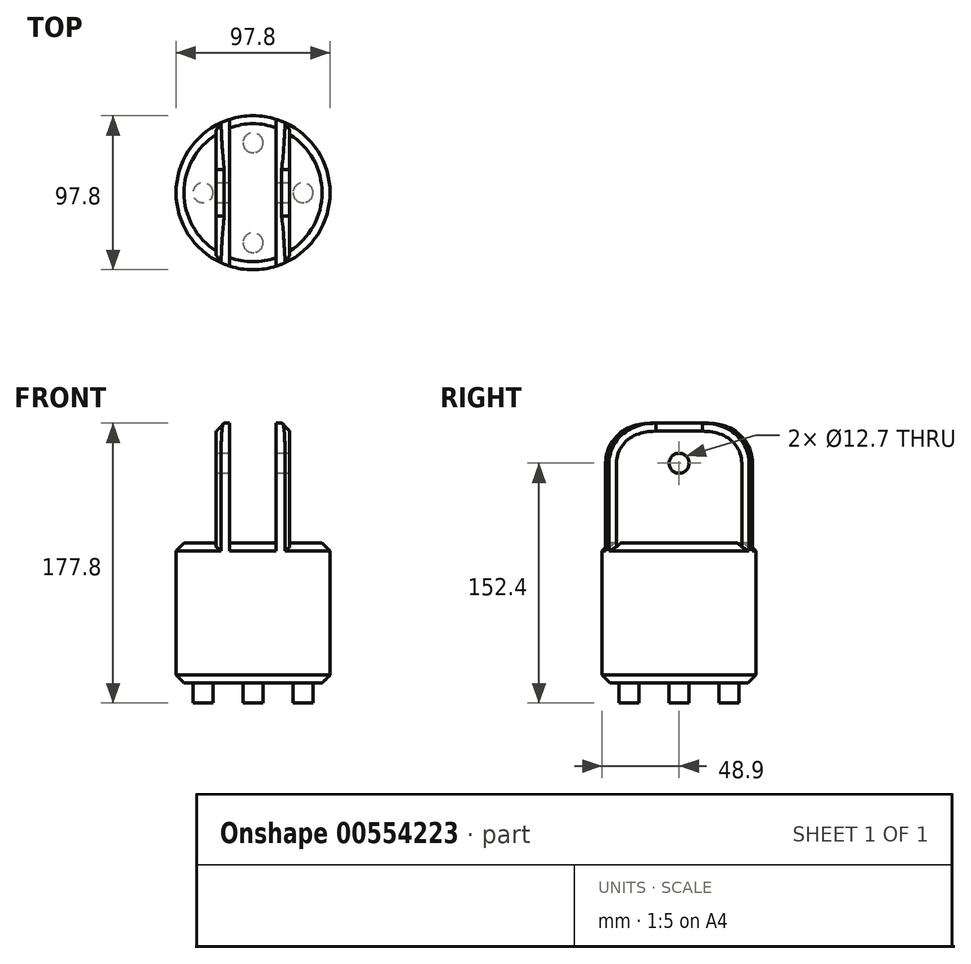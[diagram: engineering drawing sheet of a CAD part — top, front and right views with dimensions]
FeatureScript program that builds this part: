
annotation { "Feature Type Name" : "Feature", "Feature Type Description" : "" }
export const myFeature = defineFeature(function(context is Context, id is Id, definition is map)
    precondition{}
    {
        {
            var Q0;
            Q0=qCreatedBy(makeId("Top.planeOp"),FACE);
            var sketch = newSketch(context, id + "F0", { "sketchPlane" : qUnion([Q0])});
            skCircle(sketch, "E0", {"center": v(0, 0) * mm, "radius": 48.9 * mm});
            skCircle(sketch, "E1", {"center": v(0, 0) * mm, "radius": 31.75 * mm});
            skCircle(sketch, "E2", {"center": v(0, -31.75) * mm, "radius": 6.35 * mm});
            skCircle(sketch, "E3", {"center": v(-31.75, 0) * mm, "radius": 6.35 * mm});
            skCircle(sketch, "E4", {"center": v(31.75, 0) * mm, "radius": 6.35 * mm});
            skCircle(sketch, "E5", {"center": v(0, 31.75) * mm, "radius": 6.35 * mm});
            skSolve(sketch);
        }
        {
            var Q0;
            Q0=makeQuery(id+"F0.imprint","IMPRINT",FACE,{"disambiguationData":[TD([[makeQuery(id+"F0.imprint","IMPRINT",EDGE,{"derivedFrom":sQuery(id+"F0.wireOp",EDGE,"E0")}),1.0]])]});
            var Q1;
            {var subQ0=sQuery(id+"F0.wireOp",EDGE,"E3");var subQ1=sQuery(id+"F0.wireOp",EDGE,"E1");var subQ2=makeQuery(id+"F0.imprint","INTERSECT",VERTEX,{"disambiguationData":[OD(0.0)],"derivedFrom":[subQ1,subQ0]});Q1=makeQuery(id+"F0.imprint","IMPRINT",FACE,{"disambiguationData":[TD([[makeQuery(id+"F0.imprint","IMPRINT",EDGE,{"disambiguationData":[TD([[subQ2,-1.0]])],"derivedFrom":subQ1}),1.0]])]});}
            var Q2;
            {var subQ0=sQuery(id+"F0.wireOp",EDGE,"E5");var subQ1=sQuery(id+"F0.wireOp",EDGE,"E1");var subQ2=makeQuery(id+"F0.imprint","INTERSECT",VERTEX,{"disambiguationData":[OD(0.0)],"derivedFrom":[subQ1,subQ0]});Q2=makeQuery(id+"F0.imprint","IMPRINT",FACE,{"disambiguationData":[TD([[makeQuery(id+"F0.imprint","IMPRINT",EDGE,{"disambiguationData":[TD([[subQ2,-1.0]])],"derivedFrom":subQ1}),-1.0]])]});}
            var Q3;
            {var subQ0=sQuery(id+"F0.wireOp",EDGE,"E5");var subQ1=sQuery(id+"F0.wireOp",EDGE,"E1");var subQ2=makeQuery(id+"F0.imprint","INTERSECT",VERTEX,{"disambiguationData":[OD(0.0)],"derivedFrom":[subQ1,subQ0]});Q3=makeQuery(id+"F0.imprint","IMPRINT",FACE,{"disambiguationData":[TD([[makeQuery(id+"F0.imprint","IMPRINT",EDGE,{"disambiguationData":[TD([[subQ2,-1.0]])],"derivedFrom":subQ1}),1.0]])]});}
            var Q4;
            {var subQ0=sQuery(id+"F0.wireOp",EDGE,"E2");var subQ1=sQuery(id+"F0.wireOp",EDGE,"E1");var subQ2=makeQuery(id+"F0.imprint","INTERSECT",VERTEX,{"disambiguationData":[OD(0.0)],"derivedFrom":[subQ1,subQ0]});Q4=makeQuery(id+"F0.imprint","IMPRINT",FACE,{"disambiguationData":[TD([[makeQuery(id+"F0.imprint","IMPRINT",EDGE,{"disambiguationData":[TD([[subQ2,-1.0]])],"derivedFrom":subQ1}),1.0]])]});}
            var Q5;
            {var subQ0=sQuery(id+"F0.wireOp",EDGE,"E2");var subQ1=sQuery(id+"F0.wireOp",EDGE,"E1");var subQ2=makeQuery(id+"F0.imprint","INTERSECT",VERTEX,{"disambiguationData":[OD(0.0)],"derivedFrom":[subQ1,subQ0]});Q5=makeQuery(id+"F0.imprint","IMPRINT",FACE,{"disambiguationData":[TD([[makeQuery(id+"F0.imprint","IMPRINT",EDGE,{"disambiguationData":[TD([[subQ2,-1.0]])],"derivedFrom":subQ1}),-1.0]])]});}
            var Q6;
            {var subQ0=sQuery(id+"F0.wireOp",EDGE,"E4");var subQ1=sQuery(id+"F0.wireOp",EDGE,"E1");var subQ2=makeQuery(id+"F0.imprint","INTERSECT",VERTEX,{"disambiguationData":[OD(0.0)],"derivedFrom":[subQ1,subQ0]});Q6=makeQuery(id+"F0.imprint","IMPRINT",FACE,{"disambiguationData":[TD([[makeQuery(id+"F0.imprint","IMPRINT",EDGE,{"disambiguationData":[TD([[subQ2,1.0]])],"derivedFrom":subQ1}),1.0]])]});}
            var Q7;
            {var subQ0=sQuery(id+"F0.wireOp",EDGE,"E4");var subQ1=sQuery(id+"F0.wireOp",EDGE,"E1");var subQ2=makeQuery(id+"F0.imprint","INTERSECT",VERTEX,{"disambiguationData":[OD(0.0)],"derivedFrom":[subQ1,subQ0]});Q7=makeQuery(id+"F0.imprint","IMPRINT",FACE,{"disambiguationData":[TD([[makeQuery(id+"F0.imprint","IMPRINT",EDGE,{"disambiguationData":[TD([[subQ2,1.0]])],"derivedFrom":subQ1}),-1.0]])]});}
            var Q8;
            {var subQ0=sQuery(id+"F0.wireOp",EDGE,"E3");var subQ1=sQuery(id+"F0.wireOp",EDGE,"E1");var subQ2=makeQuery(id+"F0.imprint","INTERSECT",VERTEX,{"disambiguationData":[OD(0.0)],"derivedFrom":[subQ1,subQ0]});Q8=makeQuery(id+"F0.imprint","IMPRINT",FACE,{"disambiguationData":[TD([[makeQuery(id+"F0.imprint","IMPRINT",EDGE,{"disambiguationData":[TD([[subQ2,-1.0]])],"derivedFrom":subQ1}),-1.0]])]});}
            var Q9;
            {var subQ1=sQuery(id+"F0.wireOp",EDGE,"E1");var subQ8=sQuery(id+"F0.wireOp",EDGE,"E5");var subQ11=makeQuery(id+"F0.imprint","INTERSECT",VERTEX,{"disambiguationData":[OD(0.0)],"derivedFrom":[subQ1,subQ8]});Q9=makeQuery(id+"F0.imprint","IMPRINT",FACE,{"disambiguationData":[TD([[makeQuery(id+"F0.imprint","IMPRINT",EDGE,{"disambiguationData":[TD([[subQ11,1.0]])],"derivedFrom":subQ1}),1.0]])]});}
            extrude(context, id + "F1", {"entities" : qUnion([Q0, Q1, Q2, Q3, Q4, Q5, Q6, Q7, Q8, Q9]), "depth" : 88.9 * mm, "offsetDistance" : 25.4 * mm});
        }
        {
            var Q0;
            Q0=makeQuery(id+"F1.opExtrude","CAP_FACE",FACE,{"disambiguationData":[OSD([sQuery(id+"F0.wireOp",EDGE,"E0")])],"isStart":true});
            var sketch = newSketch(context, id + "F2", { "sketchPlane" : qUnion([Q0])});
            skCircle(sketch, "E6", {"center": v(-31.75, 0) * mm, "radius": 6.35 * mm});
            skCircle(sketch, "E7", {"center": v(0, 31.75) * mm, "radius": 6.35 * mm});
            skCircle(sketch, "E8", {"center": v(31.75, 0) * mm, "radius": 6.35 * mm});
            skCircle(sketch, "E9", {"center": v(0, -31.75) * mm, "radius": 6.35 * mm});
            skSolve(sketch);
        }
        {
            var Q0;
            Q0 = qSketchRegion(id + "F2", true);
            extrude(context, id + "F3", {"entities" : qUnion([Q0]), "operationType" : NewBodyOperationType.ADD, "depth" : 12.7 * mm, "offsetDistance" : 25.4 * mm});
        }
        {
            var Q0;
            Q0=makeQuery(id+"F1.opExtrude","CAP_FACE",FACE,{"disambiguationData":[OSD([sQuery(id+"F0.wireOp",EDGE,"E0")])],"isStart":false});
            var sketch = newSketch(context, id + "F4", { "sketchPlane" : qUnion([Q0])});
            skLineSegment(sketch, "E10", {"start": v(0, 0) * mm, "end": v(-19.05, 0) * mm});
            skLineSegment(sketch, "E11", {"start": v(0, 0) * mm, "end": v(19.05, 0) * mm});
            skLineSegment(sketch, "E12.bottom", {"start": v(-23.33, 46.6) * mm, "end": v(-14.77, 46.6) * mm});
            skLineSegment(sketch, "E12.top", {"start": v(-23.33, -46.6) * mm, "end": v(-14.77, -46.6) * mm});
            skLineSegment(sketch, "E12.left", {"start": v(-23.33, 46.6) * mm, "end": v(-23.33, -46.6) * mm});
            skLineSegment(sketch, "E12.right", {"start": v(-14.77, 46.6) * mm, "end": v(-14.77, -46.6) * mm});
            skPoint(sketch, "E12.middle", {"position": v(-19.05, 0) * mm});
            skLineSegment(sketch, "E13.bottom", {"start": v(14.78, 46.6) * mm, "end": v(23.32, 46.6) * mm});
            skLineSegment(sketch, "E13.top", {"start": v(14.78, -46.6) * mm, "end": v(23.32, -46.6) * mm});
            skLineSegment(sketch, "E13.left", {"start": v(14.78, 46.6) * mm, "end": v(14.78, -46.6) * mm});
            skLineSegment(sketch, "E13.right", {"start": v(23.32, 46.6) * mm, "end": v(23.32, -46.6) * mm});
            skPoint(sketch, "E13.middle", {"position": v(19.05, 0) * mm});
            skSolve(sketch);
        }
        {
            var Q0;
            Q0 = qSketchRegion(id + "F4", true);
            extrude(context, id + "F5", {"entities" : qUnion([Q0]), "operationType" : NewBodyOperationType.ADD, "depth" : 76.2 * mm, "offsetDistance" : 25.4 * mm});
        }
        {
            var Q0;
            {var subQ2=sQuery(id+"F4.wireOp",EDGE,"E12.bottom");var subQ3=sQuery(id+"F0.wireOp",EDGE,"E0");Q0=makeQuery(id+"F5.boolean.opBoolean","SPLIT",FACE,{"disambiguationData":[TD([makeQuery(id+"F5.opExtrude","SWEPT_FACE",FACE,{"disambiguationData":[OSD([subQ2])]})])],"derivedFrom":makeQuery(id+"F1.opExtrude","CAP_FACE",FACE,{"disambiguationData":[OSD([subQ3])],"isStart":false})});}
            var sketch = newSketch(context, id + "F6", { "sketchPlane" : qUnion([Q0])});
            skCircle(sketch, "E14", {"center": v(0, 0) * mm, "radius": 48.9 * mm});
            skCircle(sketch, "E15", {"center": v(0, 0) * mm, "radius": 53.8 * mm});
            skSolve(sketch);
        }
        {
            var Q0;
            Q0=makeQuery(id+"F6.imprint","IMPRINT",FACE,{"disambiguationData":[TD([[makeQuery(id+"F6.imprint","IMPRINT",EDGE,{"derivedFrom":sQuery(id+"F6.wireOp",EDGE,"E15")}),1.0]])]});
            extrude(context, id + "F7", {"entities" : qUnion([Q0]), "operationType" : NewBodyOperationType.REMOVE, "depth" : 106.17 * mm, "offsetDistance" : 25.4 * mm});
        }
        {
            var Q0;
            Q0=makeQuery(id+"F7.boolean.opBoolean","INTERSECT",EDGE,{"disambiguationData":[OD(1.0)],"derivedFrom":[makeQuery(id+"F5.opExtrude","CAP_FACE",FACE,{"disambiguationData":[OSD([sQuery(id+"F4.wireOp",EDGE,"E13.bottom"),sQuery(id+"F4.wireOp",EDGE,"E13.top"),sQuery(id+"F4.wireOp",EDGE,"E13.left"),sQuery(id+"F4.wireOp",EDGE,"E13.right")])],"isStart":false}),makeQuery(id+"F7.opExtrude","SWEPT_FACE",FACE,{"disambiguationData":[OSD([sQuery(id+"F6.wireOp",EDGE,"E14")])]})]});
            var Q1;
            Q1=makeQuery(id+"F7.boolean.opBoolean","INTERSECT",EDGE,{"disambiguationData":[OD(0.0)],"derivedFrom":[makeQuery(id+"F5.opExtrude","CAP_FACE",FACE,{"disambiguationData":[OSD([sQuery(id+"F4.wireOp",EDGE,"E13.bottom"),sQuery(id+"F4.wireOp",EDGE,"E13.top"),sQuery(id+"F4.wireOp",EDGE,"E13.left"),sQuery(id+"F4.wireOp",EDGE,"E13.right")])],"isStart":false}),makeQuery(id+"F7.opExtrude","SWEPT_FACE",FACE,{"disambiguationData":[OSD([sQuery(id+"F6.wireOp",EDGE,"E14")])]})]});
            fillet(context, id + "F8", {"entities" : qUnion([Q0, Q1]), "radius" : 25.4 * mm, "tangentPropagation" : true, "allowEdgeOverflow" : false});
        }
        {
            var Q0;
            Q0=makeQuery(id+"F7.boolean.opBoolean","INTERSECT",EDGE,{"disambiguationData":[OD(0.0)],"derivedFrom":[makeQuery(id+"F5.opExtrude","CAP_FACE",FACE,{"disambiguationData":[OSD([sQuery(id+"F4.wireOp",EDGE,"E12.bottom"),sQuery(id+"F4.wireOp",EDGE,"E12.top"),sQuery(id+"F4.wireOp",EDGE,"E12.left"),sQuery(id+"F4.wireOp",EDGE,"E12.right")])],"isStart":false}),makeQuery(id+"F7.opExtrude","SWEPT_FACE",FACE,{"disambiguationData":[OSD([sQuery(id+"F6.wireOp",EDGE,"E14")])]})]});
            var Q1;
            Q1=makeQuery(id+"F7.boolean.opBoolean","INTERSECT",EDGE,{"disambiguationData":[OD(1.0)],"derivedFrom":[makeQuery(id+"F5.opExtrude","CAP_FACE",FACE,{"disambiguationData":[OSD([sQuery(id+"F4.wireOp",EDGE,"E12.bottom"),sQuery(id+"F4.wireOp",EDGE,"E12.top"),sQuery(id+"F4.wireOp",EDGE,"E12.left"),sQuery(id+"F4.wireOp",EDGE,"E12.right")])],"isStart":false}),makeQuery(id+"F7.opExtrude","SWEPT_FACE",FACE,{"disambiguationData":[OSD([sQuery(id+"F6.wireOp",EDGE,"E14")])]})]});
            fillet(context, id + "F9", {"entities" : qUnion([Q0, Q1]), "radius" : 25.4 * mm, "tangentPropagation" : true, "allowEdgeOverflow" : false});
        }
        {
            var Q0;
            Q0=makeQuery(id+"F5.opExtrude","SWEPT_FACE",FACE,{"disambiguationData":[OSD([sQuery(id+"F4.wireOp",EDGE,"E13.right")])]});
            var sketch = newSketch(context, id + "F10", { "sketchPlane" : qUnion([Q0])});
            skLineSegment(sketch, "E16", {"start": v(0, 88.9) * mm, "end": v(0, 139.7) * mm});
            skPoint(sketch, "E16.endSnap0", {"position": v(0, 88.9) * mm});
            skCircle(sketch, "E17", {"center": v(0, 139.7) * mm, "radius": 6.35 * mm});
            skSolve(sketch);
        }
        {
            var Q0;
            Q0=makeQuery(id+"F10.imprint","IMPRINT",FACE,{"disambiguationData":[TD([[makeQuery(id+"F10.imprint","IMPRINT",EDGE,{"derivedFrom":sQuery(id+"F10.wireOp",EDGE,"E17")}),1.0]])]});
            extrude(context, id + "F11", {"entities" : qUnion([Q0]), "operationType" : NewBodyOperationType.REMOVE, "oppositeDirection" : true, "depth" : 96.52 * mm, "offsetDistance" : 25.4 * mm});
        }
        {
            var Q0;
            {var subQ0=sQuery(id+"F0.wireOp",EDGE,"E0");var subQ1=makeQuery(id+"F1.opExtrude","SWEPT_FACE",FACE,{"disambiguationData":[OSD([subQ0])]});var subQ2=makeQuery(id+"F1.opExtrude","CAP_FACE",FACE,{"disambiguationData":[OSD([subQ0])],"isStart":false});var subQ3=sQuery(id+"F4.wireOp",EDGE,"E13.right");Q0=makeQuery(id+"F5.boolean.opBoolean","SPLIT",EDGE,{"disambiguationData":[topologyDisambiguationEdgeConnected([subQ1,subQ2]),TD([makeQuery(id+"F5.opExtrude","SWEPT_FACE",FACE,{"disambiguationData":[OSD([subQ3])]})])],"derivedFrom":makeQuery(id+"F1.opExtrude","CAP_EDGE",EDGE,{"disambiguationData":[OSD([subQ0])],"isStart":false})});}
            var Q1;
            {var subQ0=sQuery(id+"F4.wireOp",EDGE,"E12.top");var subQ1=sQuery(id+"F0.wireOp",EDGE,"E0");var subQ2=makeQuery(id+"F1.opExtrude","CAP_FACE",FACE,{"disambiguationData":[OSD([subQ1])],"isStart":false});var subQ5=makeQuery(id+"F1.opExtrude","SWEPT_FACE",FACE,{"disambiguationData":[OSD([subQ1])]});Q1=makeQuery(id+"F5.boolean.opBoolean","SPLIT",EDGE,{"disambiguationData":[topologyDisambiguationEdgeConnected([subQ5,subQ2]),TD([makeQuery(id+"F5.opExtrude","SWEPT_FACE",FACE,{"disambiguationData":[OSD([subQ0])]})])],"derivedFrom":makeQuery(id+"F1.opExtrude","CAP_EDGE",EDGE,{"disambiguationData":[OSD([subQ1])],"isStart":false})});}
            var Q2;
            {var subQ0=sQuery(id+"F0.wireOp",EDGE,"E0");var subQ1=makeQuery(id+"F1.opExtrude","SWEPT_FACE",FACE,{"disambiguationData":[OSD([subQ0])]});var subQ2=makeQuery(id+"F1.opExtrude","CAP_FACE",FACE,{"disambiguationData":[OSD([subQ0])],"isStart":false});var subQ3=sQuery(id+"F4.wireOp",EDGE,"E12.left");Q2=makeQuery(id+"F5.boolean.opBoolean","SPLIT",EDGE,{"disambiguationData":[topologyDisambiguationEdgeConnected([subQ1,subQ2]),TD([makeQuery(id+"F5.opExtrude","SWEPT_FACE",FACE,{"disambiguationData":[OSD([subQ3])]})])],"derivedFrom":makeQuery(id+"F1.opExtrude","CAP_EDGE",EDGE,{"disambiguationData":[OSD([subQ0])],"isStart":false})});}
            var Q3;
            {var subQ0=sQuery(id+"F4.wireOp",EDGE,"E12.bottom");var subQ1=sQuery(id+"F0.wireOp",EDGE,"E0");var subQ2=makeQuery(id+"F1.opExtrude","CAP_FACE",FACE,{"disambiguationData":[OSD([subQ1])],"isStart":false});var subQ5=makeQuery(id+"F1.opExtrude","SWEPT_FACE",FACE,{"disambiguationData":[OSD([subQ1])]});Q3=makeQuery(id+"F5.boolean.opBoolean","SPLIT",EDGE,{"disambiguationData":[topologyDisambiguationEdgeConnected([subQ5,subQ2]),TD([makeQuery(id+"F5.opExtrude","SWEPT_FACE",FACE,{"disambiguationData":[OSD([subQ0])]})])],"derivedFrom":makeQuery(id+"F1.opExtrude","CAP_EDGE",EDGE,{"disambiguationData":[OSD([subQ1])],"isStart":false})});}
            var Q4;
            Q4=makeQuery(id+"F1.opExtrude","CAP_EDGE",EDGE,{"disambiguationData":[OSD([sQuery(id+"F0.wireOp",EDGE,"E0")])],"isStart":true});
            var Q5;
            Q5=makeQuery(id+"F7.boolean.opBoolean","INTERSECT",EDGE,{"disambiguationData":[OD(1.0)],"derivedFrom":[makeQuery(id+"F5.opExtrude","SWEPT_FACE",FACE,{"disambiguationData":[OSD([sQuery(id+"F4.wireOp",EDGE,"E12.left")])]}),makeQuery(id+"F7.opExtrude","SWEPT_FACE",FACE,{"disambiguationData":[OSD([sQuery(id+"F6.wireOp",EDGE,"E14")])]})]});
            var Q6;
            Q6=makeQuery(id+"F7.boolean.opBoolean","INTERSECT",EDGE,{"disambiguationData":[OD(1.0)],"derivedFrom":[makeQuery(id+"F5.opExtrude","SWEPT_FACE",FACE,{"disambiguationData":[OSD([sQuery(id+"F4.wireOp",EDGE,"E13.right")])]}),makeQuery(id+"F7.opExtrude","SWEPT_FACE",FACE,{"disambiguationData":[OSD([sQuery(id+"F6.wireOp",EDGE,"E14")])]})]});
            chamfer(context, id + "F12", {"entities" : qUnion([Q0, Q1, Q2, Q3, Q4, Q5, Q6]), "width" : 5.08 * mm, "tangentPropagation" : true});
        }
    });
